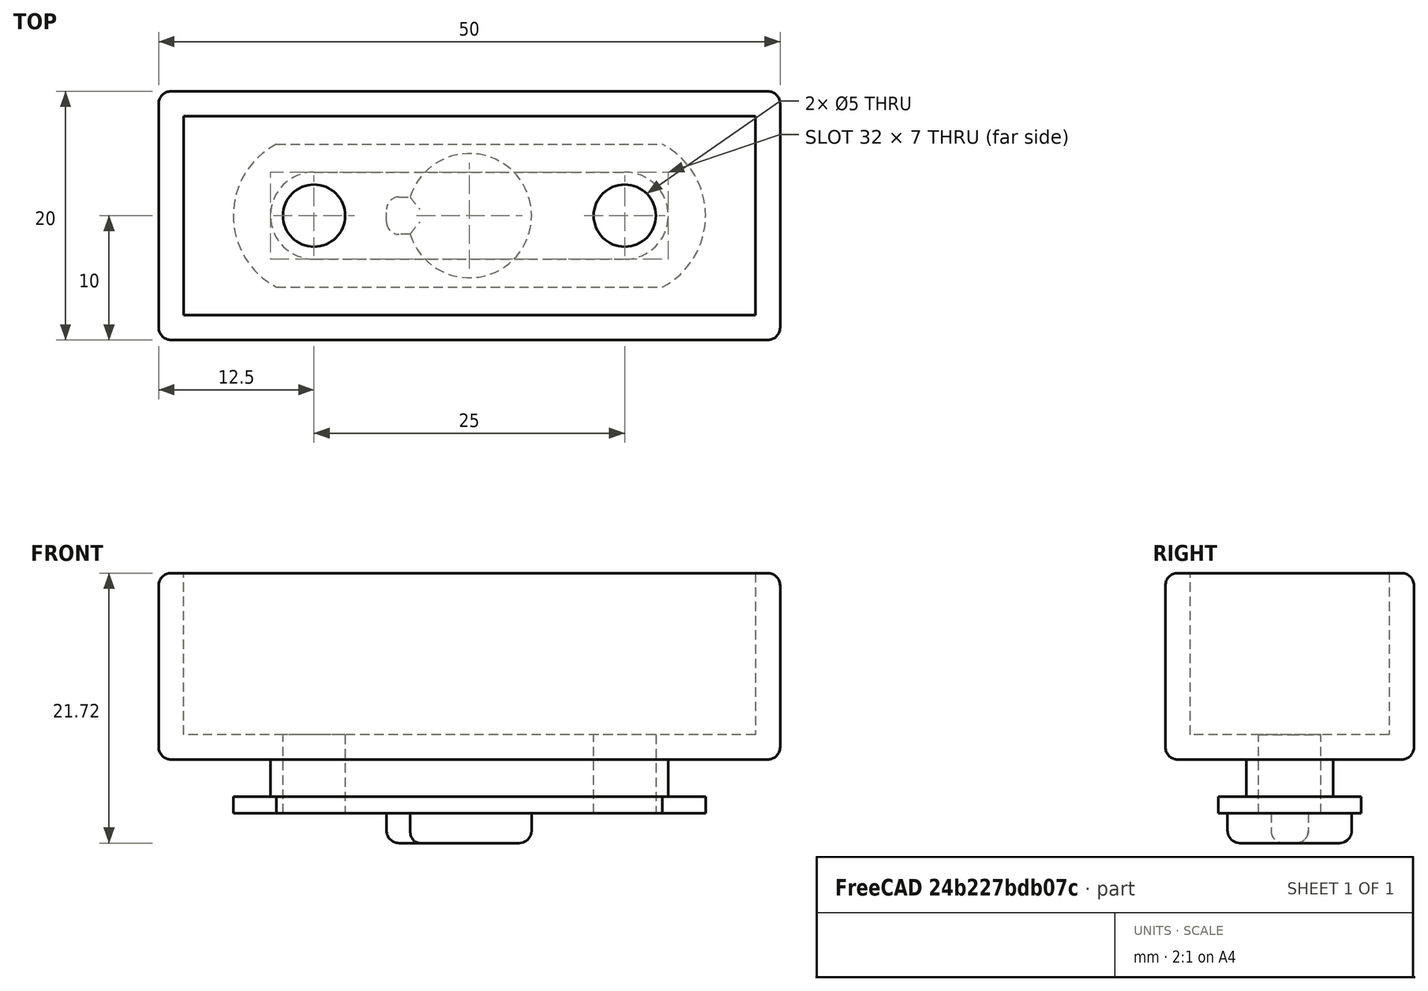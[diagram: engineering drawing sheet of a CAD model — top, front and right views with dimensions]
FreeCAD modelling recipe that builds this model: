
FCSTD DOCUMENT  (FreeCAD 0.18R15303 (Git))
Label: cable_attachment
License: Public Domain
LicenseURL: http://en.wikipedia.org/wiki/Public_domain
objects: Sketcher::SketchObject×5, PartDesign::Pad×4, PartDesign::Plane×4, PartDesign::Fillet×2, PartDesign::Thickness×1, PartDesign::Pocket×1, PartDesign::Body×1, Mesh::Feature×1
note: 23 computed .brp shape members not serialized (recipe doc carries the construction recipe); baked Part::Feature solids carry a one-line shape summary decoded from their .brp

FEATURE [Sketcher::SketchObject] Sketch
  MapMode = 5
  Support = -> [XY_Plane]
  sketch-geometry (5):
    g0: LineSegment StartX=-15.5311 StartY=5.75 StartZ=0 EndX=15.5311 EndY=5.75 EndZ=0
    g1: LineSegment StartX=-15.5311 StartY=-5.75 StartZ=0 EndX=15.5311 EndY=-5.75 EndZ=0
    g2: ArcOfCircle CenterX=-12.5 CenterY=-1.1e-15 CenterZ=0 NormalX=0 NormalY=0 NormalZ=1 AngleXU=0 Radius=6.5 StartAngle=2.05592 EndAngle=4.22726
    g3: ArcOfCircle CenterX=12.5 CenterY=-3e-16 CenterZ=0 NormalX=0 NormalY=0 NormalZ=1 AngleXU=0 Radius=6.5 StartAngle=5.19752 EndAngle=7.36885
    g4: LineSegment [constr] StartX=-19 StartY=0 StartZ=0 EndX=19 EndY=0 EndZ=0
  constraints (15):
    c: Horizontal(g1)
    c: Equal(g1,g0)
    c: Symmetric(g0,g0,g-2)
    c: DistanceY(g1,g0) = 11.5
    c: Symmetric(g0,g1,g-1)
    c: Coincident(g2,g1)
    c: Coincident(g2,g0)
    c: Coincident(g3,g0)
    c: Coincident(g3,g1)
    c: PointOnObject(g4,g-1)
    c: Symmetric(g4,g4,g-2)
    c: DistanceX(g4,g4) = 38
    c: DistanceX(g3,g4) = 6.5
    c: PointOnObject(g4,g2)
    c: PointOnObject(g4,g3)
FEATURE [PartDesign::Pad] Pad
  Length = 1.32
  Length2 = 100
  Profile = -> Sketch
  Type = 0
FEATURE [PartDesign::Plane] DatumPlane
  Length = 56.3246
  MapMode = 5
  Placement = pos=(0,0,1.32) rot=(0,0,1;0rad)
  ResizeMode = 0
  Support = -> [Pad]
  Width = 26.3246
FEATURE [Sketcher::SketchObject] Sketch001
  MapMode = 5
  Placement = pos=(0,0,1.32) rot=(0,0,1;0rad)
  Support = -> [DatumPlane]
  sketch-geometry (4):
    g0: ArcOfCircle CenterX=-12.5 CenterY=0 CenterZ=0 NormalX=0 NormalY=0 NormalZ=1 AngleXU=0 Radius=3.5 StartAngle=1.5708 EndAngle=4.7124
    g1: ArcOfCircle CenterX=12.5 CenterY=0 CenterZ=0 NormalX=0 NormalY=0 NormalZ=1 AngleXU=0 Radius=3.5 StartAngle=4.7124 EndAngle=7.85398
    g2: LineSegment StartX=-12.5 StartY=3.5 StartZ=0 EndX=12.5 EndY=3.5 EndZ=0
    g3: LineSegment StartX=-12.5 StartY=-3.5 StartZ=0 EndX=12.5 EndY=-3.5 EndZ=0
  constraints (13):
    c: PointOnObject(g0,g-1)
    c: Equal(g1,g0)
    c: DistanceX(g0,g1) = 25
    c: Symmetric(g1,g0,g-2)
    c: Diameter(g1) = 7
    c: Horizontal(g2)
    c: Horizontal(g3)
    c: Tangent(g2,g1)
    c: Coincident(g1,g3)
    c: Coincident(g1,g2)
    c: Tangent(g3,g0)
    c: Coincident(g0,g2)
    c: Coincident(g0,g3)
FEATURE [PartDesign::Pad] Pad001
  BaseFeature = -> Pad
  Length = 3
  Length2 = 100
  Profile = -> Sketch001
  Type = 0
FEATURE [PartDesign::Plane] DatumPlane001
  Length = 56.3246
  MapMode = 5
  Placement = pos=(0,0,4.32) rot=(0,0,1;0rad)
  ResizeMode = 0
  Support = -> [Pad001]
  Width = 26.3246
FEATURE [Sketcher::SketchObject] Sketch003
  MapMode = 5
  Placement = pos=(0,0,4.32) rot=(0,0,1;0rad)
  Support = -> [DatumPlane001]
  sketch-geometry (4):
    g0: LineSegment StartX=-25 StartY=10 StartZ=0 EndX=25 EndY=10 EndZ=0
    g1: LineSegment StartX=25 StartY=10 StartZ=0 EndX=25 EndY=-10 EndZ=0
    g2: LineSegment StartX=25 StartY=-10 StartZ=0 EndX=-25 EndY=-10 EndZ=0
    g3: LineSegment StartX=-25 StartY=-10 StartZ=0 EndX=-25 EndY=10 EndZ=0
  constraints (10):
    c: Coincident(g0,g1)
    c: Coincident(g1,g2)
    c: Coincident(g2,g3)
    c: Coincident(g3,g0)
    c: Horizontal(g0)
    c: Vertical(g3)
    c: DistanceX(g2,g2) = 50
    c: DistanceY(g1,g1) = 20
    c: Symmetric(g0,g1,g-1)
    c: Symmetric(g1,g2,g-2)
FEATURE [PartDesign::Pad] Pad002
  BaseFeature = -> Pad001
  Length = 15
  Length2 = 100
  Profile = -> Sketch003
  Type = 0
FEATURE [PartDesign::Thickness] Thickness
  Base = -> Pad002 [Face5]
  BaseFeature = -> Pad002
  Join = 1
  Mode = 0
  Reversed = true
  Value = 2
FEATURE [PartDesign::Plane] DatumPlane002
  Length = 56.3246
  MapMode = 5
  Placement = pos=(0,0,6.32) rot=(0,0,1;0rad)
  ResizeMode = 0
  Support = -> [Thickness]
  Width = 26.3246
FEATURE [Sketcher::SketchObject] Sketch004
  MapMode = 5
  Placement = pos=(0,0,6.32) rot=(0,0,1;0rad)
  Support = -> [DatumPlane002]
  sketch-geometry (2):
    g0: Circle CenterX=-12.5 CenterY=0 CenterZ=0 NormalX=0 NormalY=0 NormalZ=1 AngleXU=0 Radius=2.5
    g1: Circle CenterX=12.5 CenterY=0 CenterZ=0 NormalX=0 NormalY=0 NormalZ=1 AngleXU=0 Radius=2.5
  constraints (5):
    c: PointOnObject(g0,g-1)
    c: Equal(g1,g0)
    c: Symmetric(g0,g1,g-2)
    c: Diameter(g0) = 5
    c: DistanceX(g0,g1) = 25
FEATURE [PartDesign::Pocket] Pocket
  BaseFeature = -> Thickness
  Length = 5
  Length2 = 100
  Profile = -> Sketch004
  Type = 1
FEATURE [PartDesign::Fillet] Fillet
  Base = -> Pocket [Face6,Face2,Face3,Face1]
  BaseFeature = -> Pocket
  Radius = 1
FEATURE [PartDesign::Plane] DatumPlane003
  Length = 56.3246
  MapMode = 5
  Placement = pos=(0,0,0) rot=(1,0,0;3.14159rad)
  ResizeMode = 0
  Support = -> [Fillet]
  Width = 26.3246
FEATURE [Sketcher::SketchObject] Sketch005
  MapMode = 5
  Placement = pos=(0,0,0) rot=(1,0,0;3.14159rad)
  Support = -> [DatumPlane003]
  sketch-geometry (4):
    g0: ArcOfCircle CenterX=0 CenterY=0 CenterZ=0 NormalX=0 NormalY=0 NormalZ=1 AngleXU=0 Radius=5 StartAngle=3.44629 EndAngle=9.12009
    g1: LineSegment StartX=-4.7697 StartY=1.5 StartZ=0 EndX=-6.6697 EndY=1.5 EndZ=0
    g2: LineSegment StartX=-6.6697 StartY=1.5 StartZ=0 EndX=-6.6697 EndY=-1.5 EndZ=0
    g3: LineSegment StartX=-6.6697 StartY=-1.5 StartZ=0 EndX=-4.7697 EndY=-1.5 EndZ=0
  constraints (11):
    c: Coincident(g0,g-1)
    c: Diameter(g0) = 10
    c: Horizontal(g1)
    c: Coincident(g1,g2)
    c: Coincident(g2,g3)
    c: Equal(g1,g3)
    c: Symmetric(g2,g1,g-1)
    c: Coincident(g0,g3)
    c: Coincident(g0,g1)
    c: DistanceY(g2,g2) = 3
    c: DistanceX(g1,g1) = 1.9
FEATURE [PartDesign::Pad] Pad003
  BaseFeature = -> Fillet
  Length = 2.4
  Length2 = 100
  Profile = -> Sketch005
  Type = 0
FEATURE [PartDesign::Fillet] Fillet001
  Base = -> Pad003 [Edge106,Edge108,Edge109,Edge105,Edge110,Edge107]
  BaseFeature = -> Pad003
  Radius = 1
FEATURE [PartDesign::Body] Body
  Group = -> [Sketch,Pad,DatumPlane,Sketch001,Pad001,DatumPlane001,Sketch003,Pad002,Thickness,DatumPlane002,Sketch004,Pocket,Fillet,DatumPlane003,Sketch005,Pad003,Fillet001]
  Origin = -> Origin
  Tip = -> Fillet001
FEATURE [Mesh::Feature] Mesh  label="Fillet001 (Meshed)"
